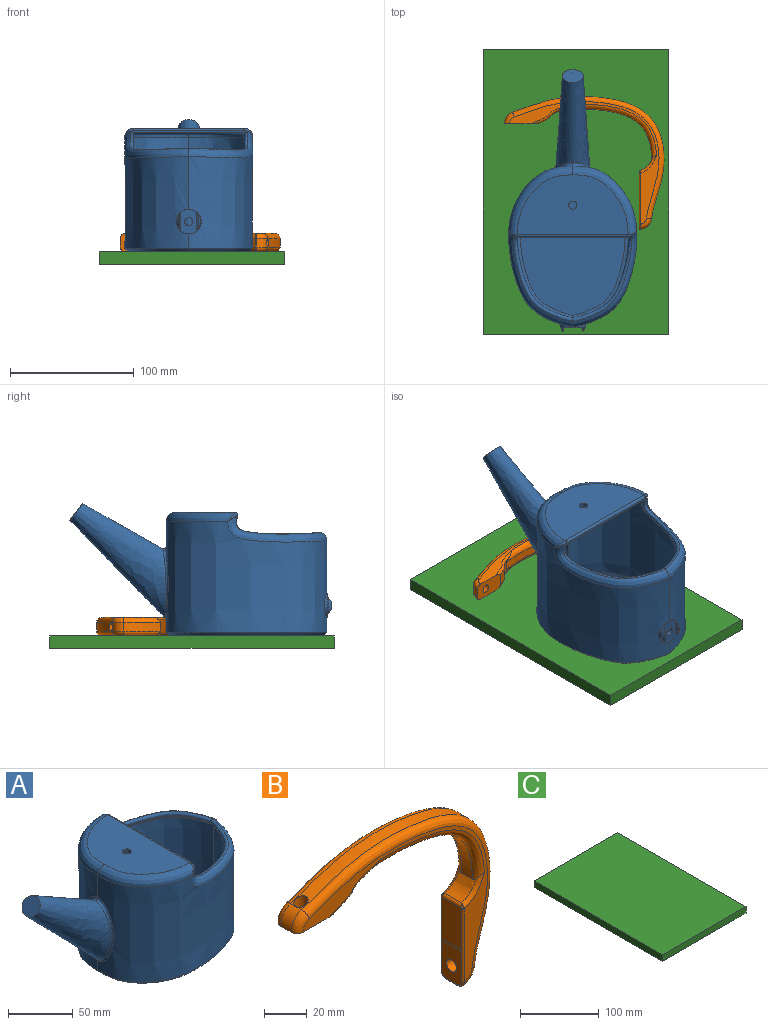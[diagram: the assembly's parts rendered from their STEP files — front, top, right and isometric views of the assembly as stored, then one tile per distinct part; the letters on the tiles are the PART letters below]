
ASSEMBLY  parts=3 mates=2
PART A: 61 faces, bbox 301.5x176.1x233.7 mm
  f0: cylinder r=6.5mm len=11.7mm, axis (1,0,0), area 0mm2, adj f1,f60
  f1: bspline ~13.98x5.16mm, area 21.1mm2, adj f0,f2,f58,f59
  f2: bspline ~3.63x1.7mm, area 3.8mm2, adj f1,f3,f58,f60
  f3: bspline ~4.31x2.08mm, area 3.8mm2, adj f2,f4,f56,f60
  f4: extruded ~123x83.5mm, area 12550.4mm2, adj f3,f5,f6,f47,f48,f49,f54,f55
  f5: bspline ~3.63x1.7mm, area 3.8mm2, adj f4,f56,f59,f60
  f6: bspline ~76.38x48.62mm, area 594.6mm2, adj f4,f7,f45,f46,f47
  f7: plane 95.09x50.8mm, normal (0,0,-1), area 3655mm2, adj f6,f8,f38,f39,f40,f41,f42,f43
  f8: bspline ~80.18x52.44mm, area 914.3mm2, adj f7,f9,f35,f36,f37,f38,f42,f43
  f9: bspline ~2.08x2.03mm, area 0.9mm2, adj f8,f10,f34,f35
  f10: plane 89.84x48.69mm, normal (0,0,1), area 3476.7mm2, adj f9,f11,f13,f33,f34,f44
  f11: bspline ~2.05x2.03mm, area 0.9mm2, adj f10,f12,f34,f42
  f12: bspline ~8.23x7.84mm, area 16.4mm2, adj f11,f13,f42
  f13: bspline ~57.15x52.69mm, area 863.7mm2, adj f10,f12,f14,f33
  f14: extruded ~130x90mm, area 14186.5mm2, adj f13,f15,f19,f22,f36,f42
  f15: bspline ~59.66x17.03mm, area 185.4mm2, adj f14,f16,f17
  f16: bspline ~59.68x17.12mm, area 185.3mm2, adj f15,f17,f36
  f17: bspline ~111.58x96.67mm, area 7654.5mm2, adj f15,f16,f18
  f18: plane 88.52x85mm, normal (-0.79,0,0.61), area 149mm2, adj f17,f48
  f19: bspline ~130x51.97mm, area 769.7mm2, adj f14,f20,f21
  f20: plane 124.68x98.82mm, normal (0,0,-1), area 9735mm2, adj f19,f21
  f21: bspline ~130x51.97mm, area 769.6mm2, adj f19,f20,f36
  f22: cylinder r=10mm len=20mm, axis (1,0,0), area 110.7mm2, adj f14,f23,f27,f31,f36
  f23: cone r=10mm half-angle=30deg, axis (-1,0,0), area 17mm2, adj f22,f24,f26
  f24: cylinder r=1mm len=15.2mm, axis (0,0,1), area 20.9mm2, adj f23,f25,f31
  f25: plane 11.42x2.25mm, normal (0,-1,0), area 17.9mm2, adj f24,f26
  f26: torus R=2.49mm, axis (1,0,0), area 24.1mm2, adj f23,f25
  f27: cone r=10mm half-angle=30deg, axis (-1,0,0), area 17mm2, adj f22,f28,f30
  f28: torus R=2.49mm, axis (1,0,0), area 24.1mm2, adj f27,f29
  f29: plane 11.42x2.25mm, normal (0,1,0), area 17.9mm2, adj f28,f30
  f30: cylinder r=1mm len=15.2mm, axis (0,0,-1), area 20.9mm2, adj f27,f29,f31
  f31: plane 20x13mm, normal (1,0,0), area 206.1mm2, adj f22,f24,f30,f32
  f32: cylinder r=3.3mm len=6.6mm, axis (1,0,0), area 72.6mm2, adj f31,f60
  f33: bspline ~57.15x52.69mm, area 863.7mm2, adj f10,f13,f35,f36
  f34: cylinder r=2mm len=89.36mm, axis (0,-1,0), area 283.5mm2, adj f9,f10,f11,f43
  f35: bspline ~8.23x7.84mm, area 16.5mm2, adj f8,f9,f33
  f36: extruded ~130x90mm, area 14186.5mm2, adj f8,f14,f16,f21,f22,f33
  f37: bspline ~3.05x2.92mm, area 0.1mm2, adj f8,f38,f41,f45
  f38: bspline ~70.24x54.43mm, area 395.1mm2, adj f7,f8,f37,f39
  f39: bspline ~68.84x44.93mm, area 109.5mm2, adj f7,f38,f45,f46
  f40: bspline ~53.63x49.19mm, area 409.1mm2, adj f7,f46,f47,f58
  f41: bspline ~70.24x47.82mm, area 395.1mm2, adj f7,f37,f42,f45
  f42: bspline ~80.17x52.42mm, area 914.8mm2, adj f7,f8,f11,f12,f14,f41,f43
  f43: extruded ~89.36x1.47mm, area 131.3mm2, adj f7,f8,f34,f42
  f44: cylinder r=3.3mm len=6.6mm, axis (0,0,1), area 72.6mm2, adj f7,f10
  f45: bspline ~68.84x44.93mm, area 109.5mm2, adj f6,f7,f37,f39,f41
  f46: bspline ~76.38x48.75mm, area 594.6mm2, adj f6,f7,f39,f40,f58
  f47: bspline ~53.63x49.19mm, area 409.1mm2, adj f4,f6,f7,f40
  f48: offset ~169.18x134.13mm, area 12957mm2, adj f4,f18,f58
  f49: bspline ~123.11x52.82mm, area 1583.2mm2, adj f4,f50,f53,f54
  f50: bspline ~123.11x52.82mm, area 1583mm2, adj f49,f51,f53,f58
  f51: bspline ~6x6mm, area 1.2mm2, adj f50,f52,f58
  f52: bspline ~6.01x6mm, area 0.8mm2, adj f51,f53,f55,f58
  f53: plane 111.04x84.85mm, normal (0,0,1), area 7533.8mm2, adj f49,f50,f52,f55
  f54: bspline ~6x6mm, area 1.5mm2, adj f4,f49,f55
  f55: bspline ~6.01x6mm, area 0.8mm2, adj f4,f52,f53,f54
  f56: bspline ~14.3x5.47mm, area 21.1mm2, adj f3,f4,f5,f57
  f57: cylinder r=6.5mm len=11.7mm, axis (1,0,0), area 0mm2, adj f56,f60
  f58: extruded ~123x83.5mm, area 12550.4mm2, adj f1,f2,f4,f40,f46,f48,f50,f51
  f59: bspline ~4.31x2.08mm, area 3.8mm2, adj f1,f5,f58,f60
  f60: plane 13.03x13.03mm, normal (-1,0,0), area 98.5mm2, adj f0,f2,f3,f5,f32,f57,f59
PART B: 36 faces, bbox 158.7x16.2x142.9 mm
  f0: plane 23.61x13mm, normal (-1,0,0), area 306.9mm2, adj f1,f22,f23,f27,f30,f31
  f1: extruded ~13x1.36mm, area 17.7mm2, adj f0,f2,f22,f23
  f2: plane 19.96x13mm, normal (-1,0,0), area 221.4mm2, adj f1,f13,f22,f23,f24,f25,f26
  f3: cylinder r=10mm len=8.81mm, axis (0,1,0), area 84.1mm2, adj f4,f13,f14,f17,f26
  f4: extruded ~122.56x98.79mm, area 1359mm2, adj f3,f5,f12,f13,f15,f18
  f5: cylinder r=10mm len=9.43mm, axis (0,1,0), area 86.3mm2, adj f4,f6,f16,f19
  f6: plane 27.35x16.16mm, normal (0,0,-1), area 347.3mm2, adj f5,f7,f10,f11,f12,f16,f19,f34
  f7: extruded ~21.78x11.68mm, area 242mm2, adj f6,f8,f20,f21,f34,f35
  f8: extruded ~74.88x41.64mm, area 696.2mm2, adj f7,f9,f20,f21
  f9: extruded ~11x9.45mm, area 138.7mm2, adj f8,f20,f21,f28,f30,f33
  f10: plane 121.25x99.52mm, normal (0,-1,0), area 976mm2, adj f6,f17,f18,f19,f21,f22,f33,f35
  f11: plane 121.26x99.52mm, normal (0,1,0), area 976.5mm2, adj f6,f14,f15,f16,f20,f23,f28,f34
  f12: cylinder r=3.3mm len=11.83mm, axis (0,0,1), area 245.3mm2, adj f4,f6
  f13: cylinder r=3.3mm len=9.92mm, axis (1,0,0), area 203.9mm2, adj f2,f3,f4
  f14: torus R=6mm, axis (0,-1,0), area 70.4mm2, adj f3,f11,f15,f25
  f15: bspline ~157.54x141.78mm, area 1256.8mm2, adj f4,f11,f14,f16
  f16: torus R=6mm, axis (0,-1,0), area 66.2mm2, adj f5,f6,f11,f15
  f17: torus R=6mm, axis (0,-1,0), area 70.4mm2, adj f3,f10,f18,f24
  f18: bspline ~157.54x141.78mm, area 1256.7mm2, adj f4,f10,f17,f19
  f19: torus R=6mm, axis (0,-1,0), area 66.2mm2, adj f5,f6,f10,f18
  f20: bspline ~80.38x46.38mm, area 594.3mm2, adj f7,f8,f9,f11,f28,f34
  f21: bspline ~80.38x46.38mm, area 594.3mm2, adj f7,f8,f9,f10,f33,f35
  f22: cylinder r=1mm len=41.53mm, axis (0,0,1), area 65mm2, adj f0,f1,f2,f10,f24,f31
  f23: cylinder r=1mm len=41.53mm, axis (0,0,-1), area 65mm2, adj f0,f1,f2,f11,f25,f27
  f24: bspline ~5.07x4.92mm, area 9.5mm2, adj f2,f17,f22,f26
  f25: bspline ~4.92x4.38mm, area 9.5mm2, adj f2,f14,f23,f26
  f26: cylinder r=1mm len=7mm, axis (0,1,0), area 11.8mm2, adj f2,f3,f24,f25
  f27: bspline ~1.61x1.2mm, area 0.9mm2, adj f0,f23,f28,f29
  f28: bspline ~26.16x19.45mm, area 52.5mm2, adj f9,f11,f20,f27,f29
  f29: bspline ~2.18x1.96mm, area 1.4mm2, adj f27,f28,f30
  f30: cylinder r=2mm len=12.87mm, axis (0,1,0), area 28.6mm2, adj f0,f9,f29,f32
  f31: bspline ~1.61x1.2mm, area 0.9mm2, adj f0,f22,f32,f33
  f32: bspline ~2.18x1.96mm, area 1.4mm2, adj f30,f31,f33
  f33: bspline ~26.16x19.45mm, area 52.5mm2, adj f9,f10,f21,f31,f32
  f34: bspline ~38.87x19.29mm, area 98.8mm2, adj f6,f7,f11,f20
  f35: bspline ~38.87x19.29mm, area 98.8mm2, adj f6,f7,f10,f21
PART C: 6 faces, bbox 150x230x10 mm
  f0: plane 230x10mm, normal (-1,0,0), area 2300mm2, adj f1,f3,f4,f5
  f1: plane 150x10mm, normal (0,-1,0), area 1500mm2, adj f0,f2,f4,f5
  f2: plane 230x10mm, normal (1,0,0), area 2300mm2, adj f1,f3,f4,f5
  f3: plane 150x10mm, normal (0,1,0), area 1500mm2, adj f0,f2,f4,f5
  f4: plane 230x150mm, normal (0,0,1), area 34500mm2, adj f0,f1,f2,f3
  f5: plane 230x150mm, normal (0,0,-1), area 34500mm2, adj f0,f1,f2,f3
PLACE A rot(axis=(0,0,-1),90deg) t=(-215.4,-6.23,6.41)mm
PLACE B rot(axis=(-1,0,0),90deg) t=(-234.74,-14.35,13.91)mm
PLACE C t=(0,0,-3.59)mm fixed
MATE planar A.f20 <-> C.f4  axis (0,0,-1) through (-215.4,-12.11,6.41)mm
MATE planar B.f11 <-> C.f4  axis (0,0,-1) through (-189.37,65.44,6.41)mm
